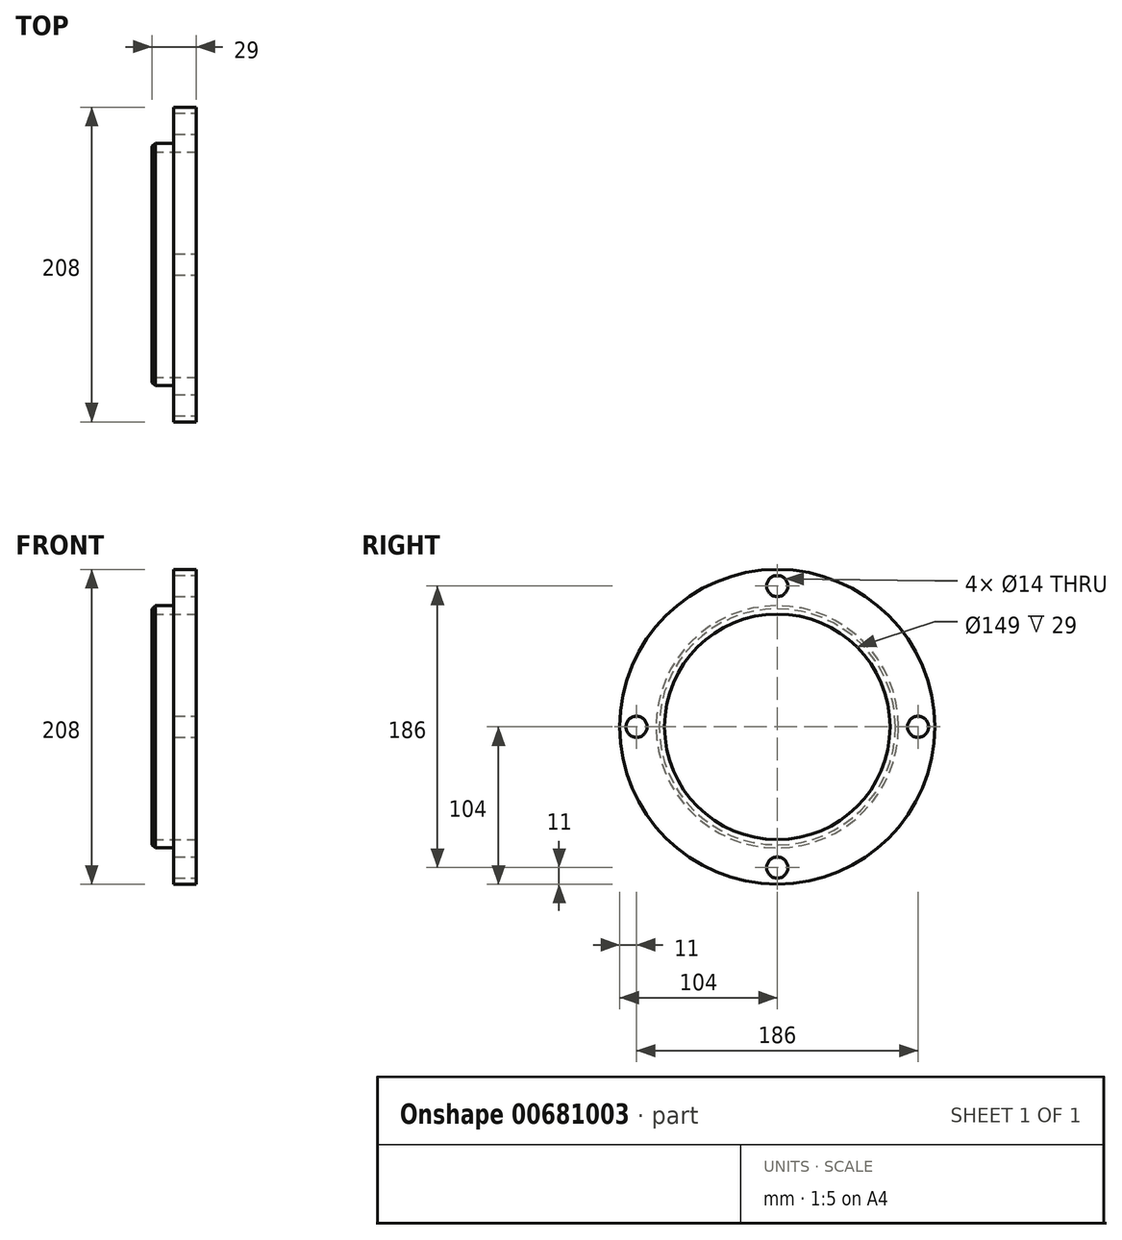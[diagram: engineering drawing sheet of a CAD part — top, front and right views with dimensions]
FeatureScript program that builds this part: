
annotation { "Feature Type Name" : "Feature", "Feature Type Description" : "" }
export const myFeature = defineFeature(function(context is Context, id is Id, definition is map)
    precondition{}
    {
        {
            var Q0;
            Q0=qCreatedBy(makeId("Right.planeOp"),FACE);
            var sketch = newSketch(context, id + "F0", { "sketchPlane" : qUnion([Q0])});
            skCircle(sketch, "E0", {"center": v(0, 0) * mm, "radius": 104 * mm});
            skSolve(sketch);
        }
        {
            var Q0;
            Q0=qSketchRegion(id+"F0",true);
            extrude(context, id + "F1", {"entities" : qUnion([Q0]), "depth" : (29 - 14.1) * mm, "offsetDistance" : 25 * mm});
        }
        {
            var Q0;
            Q0=makeQuery(id+"F1.opExtrude","CAP_FACE",FACE,{"disambiguationData":[OSD([sQuery(id+"F0.wireOp",EDGE,"E0")])],"isStart":true});
            var sketch = newSketch(context, id + "F2", { "sketchPlane" : qUnion([Q0])});
            skCircle(sketch, "E1", {"center": v(0, 0) * mm, "radius": 80 * mm});
            skSolve(sketch);
        }
        {
            var Q0;
            Q0=qSketchRegion(id+"F2",true);
            extrude(context, id + "F3", {"entities" : qUnion([Q0]), "operationType" : NewBodyOperationType.ADD, "depth" : 14.1 * mm, "offsetDistance" : 25 * mm});
        }
        {
            var Q0;
            Q0=makeQuery(id+"F3.opExtrude","CAP_EDGE",EDGE,{"disambiguationData":[OSD([sQuery(id+"F2.wireOp",EDGE,"E1")])],"isStart":false});
            chamfer(context, id + "F4", {"entities" : qUnion([Q0]), "width" : 2 * mm, "tangentPropagation" : true});
        }
        {
            var Q0;
            Q0=makeQuery(id+"F1.opExtrude","CAP_FACE",FACE,{"disambiguationData":[OSD([sQuery(id+"F0.wireOp",EDGE,"E0")])],"isStart":false});
            var sketch = newSketch(context, id + "F5", { "sketchPlane" : qUnion([Q0])});
            skPoint(sketch, "E2", {"position": v(0, 0) * mm});
            skSolve(sketch);
        }
        {
            var Q0;
            Q0=sQuery(id+"F5.wireOp",VERTEX,"E2");
            var Q1;
            Q1=makeQuery(id+"F1.opExtrude","SWEPT_BODY",BODY,{"disambiguationData":[OSD([sQuery(id+"F0.wireOp",EDGE,"E0")])]});
            hole(context, id + "F6", {"style" : HoleStyle.SIMPLE, "endStyle" : HoleEndStyle.THROUGH, "holeDiameter" : 149 * mm, "majorDiameter" : 5 * mm, "isTappedThrough" : true, "tappedDepth" : 24.75 * mm, "tapClearance" : 3, "locations" : qUnion([Q0]), "scope" : qUnion([Q1])});
        }
        {
            var Q0;
            Q0=makeQuery(id+"F1.opExtrude","CAP_FACE",FACE,{"disambiguationData":[OSD([sQuery(id+"F0.wireOp",EDGE,"E0")])],"isStart":false});
            var sketch = newSketch(context, id + "F7", { "sketchPlane" : qUnion([Q0])});
            skCircle(sketch, "E3", {"center": v(0, 0) * mm, "radius": 93 * mm, "construction": true});
            skLineSegment(sketch, "E4", {"start": v(0, 0) * mm, "end": v(115.14, 0) * mm, "construction": true});
            skPoint(sketch, "E5", {"position": v(93, 0) * mm});
            skPoint(sketch, "E6.1.0", {"position": v(0, 93) * mm});
            skPoint(sketch, "E6.2.0", {"position": v(-93, 0) * mm});
            skPoint(sketch, "E6.3.0", {"position": v(0, -93) * mm});
            skSolve(sketch);
        }
        {
            var Q0;
            Q0=sQuery(id+"F7.wireOp",VERTEX,"E5");
            var Q1;
            Q1=sQuery(id+"F7.wireOp",VERTEX,"E6.3.0");
            var Q2;
            Q2=sQuery(id+"F7.wireOp",VERTEX,"E6.2.0");
            var Q3;
            Q3=sQuery(id+"F7.wireOp",VERTEX,"E6.1.0");
            var Q4;
            Q4=makeQuery(id+"F1.opExtrude","SWEPT_BODY",BODY,{"disambiguationData":[OSD([sQuery(id+"F0.wireOp",EDGE,"E0")])]});
            hole(context, id + "F8", {"style" : HoleStyle.SIMPLE, "endStyle" : HoleEndStyle.THROUGH, "holeDiameter" : 14 * mm, "majorDiameter" : 5 * mm, "isTappedThrough" : true, "tappedDepth" : 24.75 * mm, "tapClearance" : 3, "locations" : qUnion([Q0, Q1, Q2, Q3]), "scope" : qUnion([Q4])});
        }
    });
